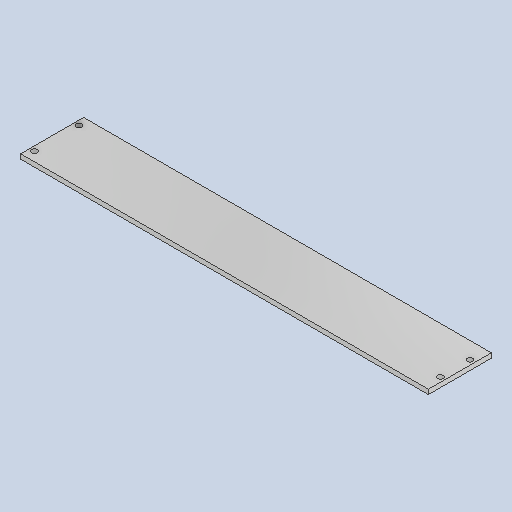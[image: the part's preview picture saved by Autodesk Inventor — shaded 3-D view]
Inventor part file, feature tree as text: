
AUTODESK INVENTOR PART (.ipt)
format: ipt  version: 2025.1 (Build 291241020, 241B)  size: 109,568 bytes
history: native  units: in
note: dims shown in document units (in); Inventor stores cm internally (conversion verified against a paired STEP export)
features: sketch x2, extrude x1, hole x1, projected_geometry x1
ambient origin geometry x8: Origin, YZ Plane, XZ Plane, XY Plane, X Axis, Y Axis, Z Axis, Center Point
bodies: Solid1 (feature_tree)
feature tree (5):
  sketch  "Sketch10"  dims[d48=11.0in d49=1.7in]
  extrude  "Extrusion8"  Depth=1.7in
  hole  "Hole2"  [1 undecoded]
  sketch  "Sketch11"  dims[d51=5.5in d52=0.125in d53=0.0in d54=0.45in d55=0.125in d56=0.45in d57=0.125in d58=0.125in d59=0.125in d60=0.25in d61=0.25in d62=0.15in d63=0.75in d64=0.375in d65=0.25in d66=0.5635in d67=1.0in d68=0.8108in]
  projected_geometry  "Projected Loop2"
note: 1 required parameter value undecoded (feature->parameter linkage not recoverable at this tier; creation-order binding heuristic only, values carry confidence <= 0.55)
